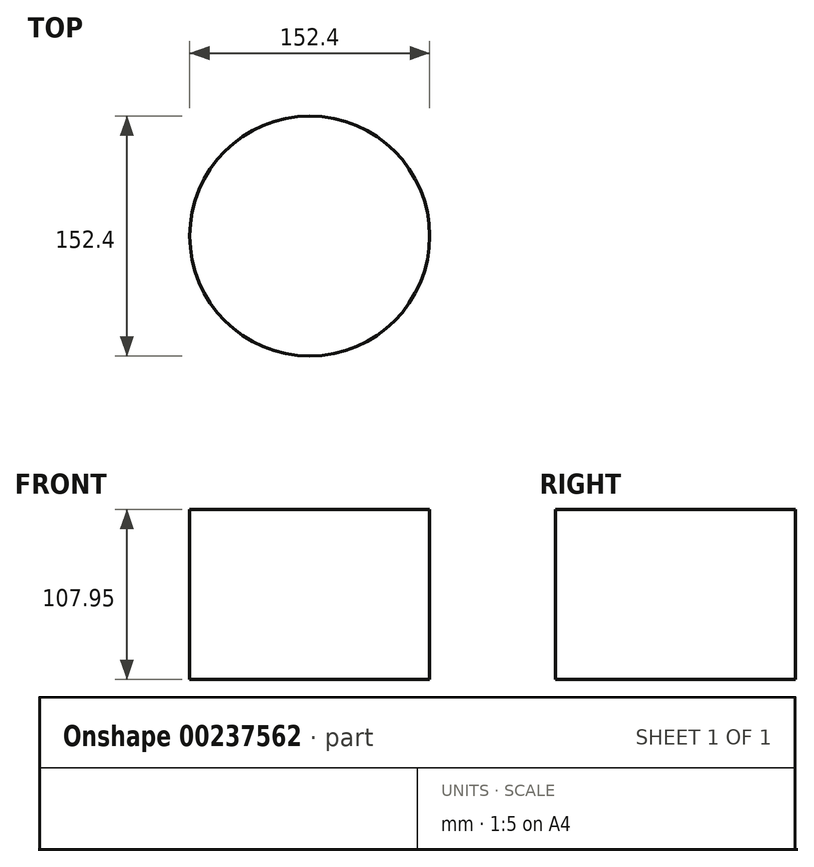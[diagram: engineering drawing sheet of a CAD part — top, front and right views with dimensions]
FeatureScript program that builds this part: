
annotation { "Feature Type Name" : "Feature", "Feature Type Description" : "" }
export const myFeature = defineFeature(function(context is Context, id is Id, definition is map)
    precondition{}
    {
        {
            var Q0;
            Q0=qCreatedBy(makeId("Top.planeOp"),FACE);
            var sketch = newSketch(context, id + "F0", { "sketchPlane" : qUnion([Q0])});
            skCircle(sketch, "E0", {"center": v(0, 0) * mm, "radius": 76.2 * mm});
            skSolve(sketch);
        }
        {
            var Q0;
            Q0 = qSketchRegion(id + "F0", true);
            extrude(context, id + "F1", {"entities" : qUnion([Q0]), "depth" : 107.95 * mm});
        }
    });
